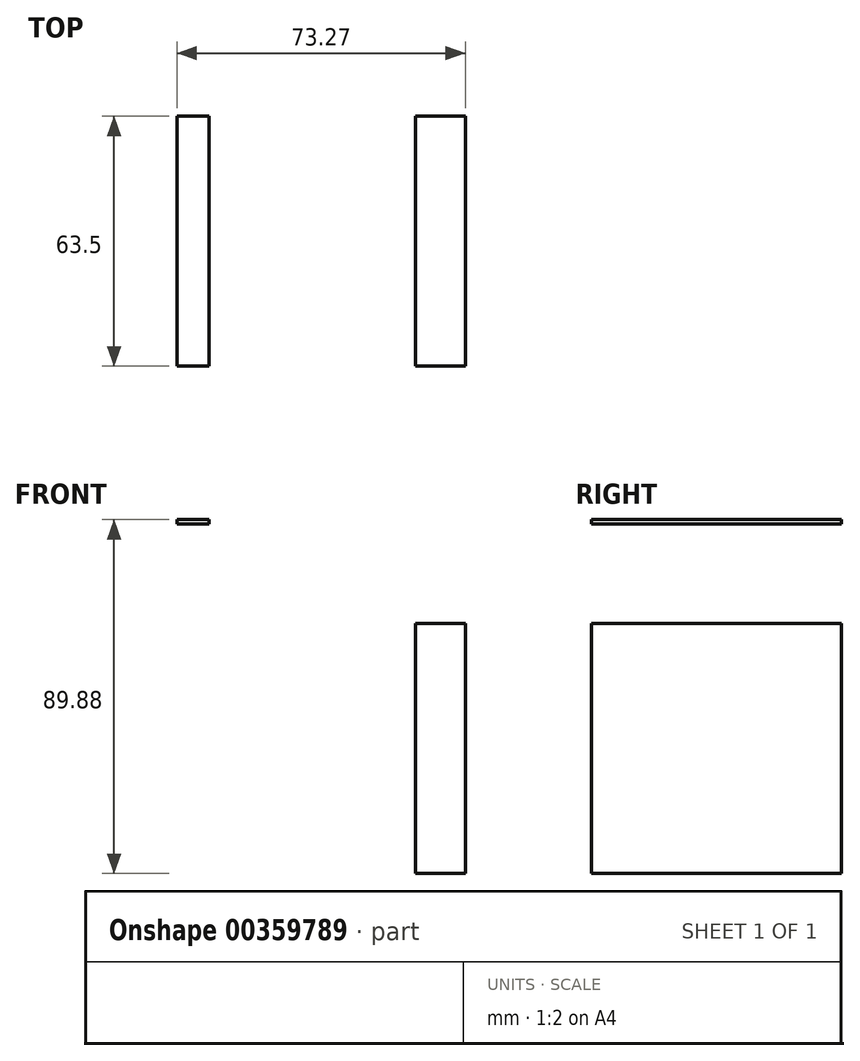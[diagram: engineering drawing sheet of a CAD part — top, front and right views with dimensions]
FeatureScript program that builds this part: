
annotation { "Feature Type Name" : "Feature", "Feature Type Description" : "" }
export const myFeature = defineFeature(function(context is Context, id is Id, definition is map)
    precondition{}
    {
        {
            var Q0;
            Q0=qCreatedBy(makeId("Front.planeOp"),FACE);
            var sketch = newSketch(context, id + "F0", { "sketchPlane" : qUnion([Q0])});
            skLineSegment(sketch, "E0.bottom", {"start": v(0, 0) * mm, "end": v(12.7, 0) * mm});
            skLineSegment(sketch, "E0.top", {"start": v(0, -63.5) * mm, "end": v(12.7, -63.5) * mm});
            skLineSegment(sketch, "E0.left", {"start": v(0, 0) * mm, "end": v(0, -63.5) * mm});
            skLineSegment(sketch, "E0.right", {"start": v(12.7, 0) * mm, "end": v(12.7, -63.5) * mm});
            skLineSegment(sketch, "E1.bottom", {"start": v(-52.43, 26.38) * mm, "end": v(-60.57, 26.38) * mm});
            skLineSegment(sketch, "E1.top", {"start": v(-52.43, 25.24) * mm, "end": v(-60.57, 25.24) * mm});
            skLineSegment(sketch, "E1.left", {"start": v(-52.43, 26.38) * mm, "end": v(-52.43, 25.24) * mm});
            skLineSegment(sketch, "E1.right", {"start": v(-60.57, 26.38) * mm, "end": v(-60.57, 25.24) * mm});
            skSolve(sketch);
        }
        {
            var Q0;
            Q0 = qSketchRegion(id + "F0", true);
            extrude(context, id + "F1", {"entities" : qUnion([Q0]), "depth" : 63.5 * mm});
        }
    });
